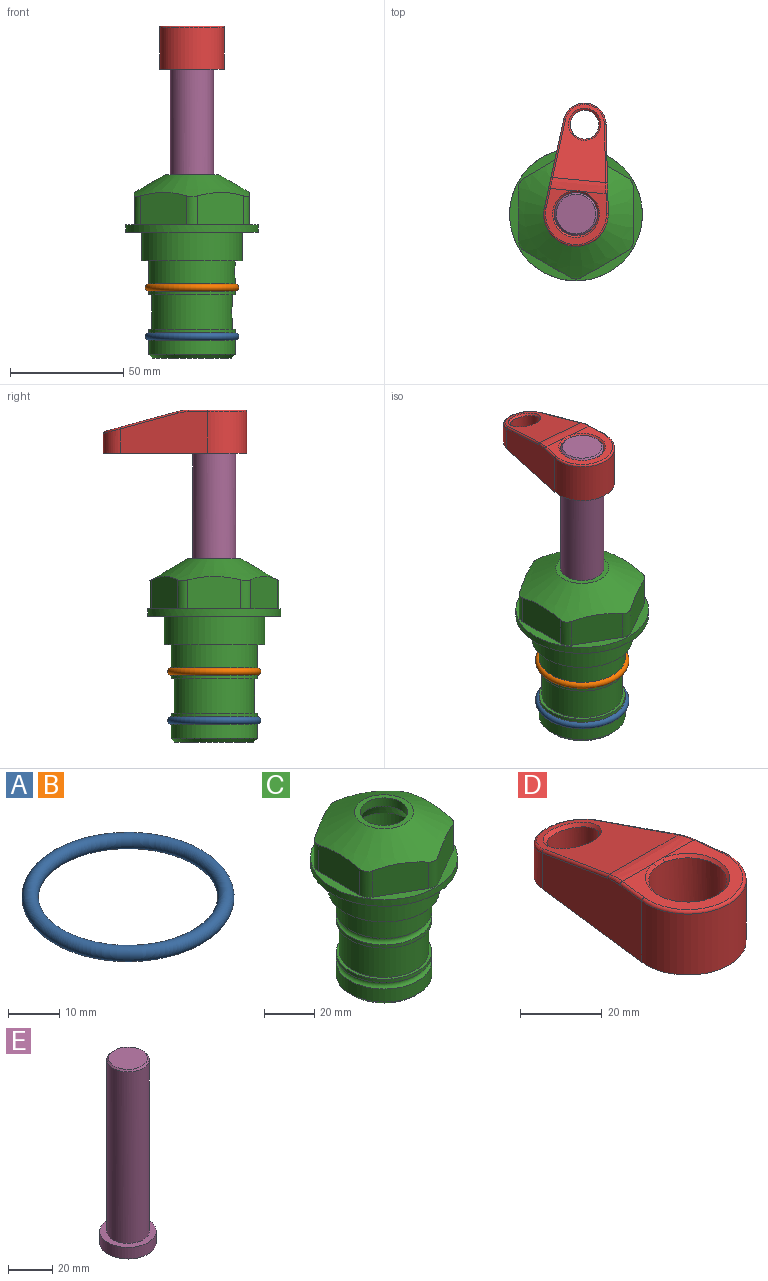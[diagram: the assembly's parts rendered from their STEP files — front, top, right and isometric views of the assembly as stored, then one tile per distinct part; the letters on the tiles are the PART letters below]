
ASSEMBLY  parts=5 mates=4
PART A: 1 faces, bbox 44.7x44.7x3.2 mm
  f0: torus R=19.05mm, axis (0,0,1), area 1193.9mm2
PART B: same geometry as A
PART C: 36 faces, bbox 58.7x58.7x81 mm
  f0: cylinder r=17.78mm len=35.56mm, axis (0,0,1), area 1670.8mm2, adj f23,f24,f31
  f1: cylinder r=19.05mm len=38.1mm, axis (0,0,1), area 1191.9mm2, adj f26,f27,f30
  f2: plane 58.66x58.66mm, normal (0,0,-1), area 1150.6mm2, adj f3,f28
  f3: cylinder r=29.33mm len=58.66mm, axis (0,0,-1), area 585.1mm2, adj f2,f4
  f4: plane 58.66x58.66mm, normal (0,0,1), area 475.9mm2, adj f3,f5,f6,f7,f8,f9,f10,f11
  f5: plane 20.32x14.34mm, normal (-0.5,0.87,0), area 324.4mm2, adj f4,f15,f16,f17
  f6: plane 20.32x14.34mm, normal (0.5,0.87,0), area 324.4mm2, adj f4,f14,f15,f17
  f7: plane 23.48x14.34mm, normal (1,0,0), area 324.4mm2, adj f4,f13,f14,f17
  f8: plane 20.32x14.34mm, normal (0.5,-0.87,0), area 324.4mm2, adj f4,f12,f13,f17
  f9: plane 20.32x14.34mm, normal (-0.5,-0.87,0), area 324.4mm2, adj f4,f11,f12,f17
  f10: plane 23.48x14.34mm, normal (-1,0,0), area 324.4mm2, adj f4,f11,f16,f17
  f11: cylinder r=5.08mm len=12.85mm, axis (0,0,-1), area 67.2mm2, adj f4,f9,f10,f17
  f12: cylinder r=5.08mm len=12.85mm, axis (0,0,-1), area 67.2mm2, adj f4,f8,f9,f17
  f13: cylinder r=5.08mm len=12.85mm, axis (0,0,-1), area 67.2mm2, adj f4,f7,f8,f17
  f14: cylinder r=5.08mm len=12.85mm, axis (0,0,-1), area 67.2mm2, adj f4,f6,f7,f17
  f15: cylinder r=5.08mm len=12.85mm, axis (0,0,-1), area 67.2mm2, adj f4,f5,f6,f17
  f16: cylinder r=5.08mm len=12.85mm, axis (0,0,-1), area 67.2mm2, adj f4,f5,f10,f17
  f17: cone r=11.73mm half-angle=60deg, axis (0,0,-1), area 2071.8mm2, adj f5,f6,f7,f8,f9,f10,f11,f12
  f18: plane 23.46x23.46mm, normal (0,0,1), area 147.4mm2, adj f17,f35
  f19: plane 34.93x34.93mm, normal (0,0,-1), area 958mm2, adj f29
  f20: cylinder r=19.05mm len=38.1mm, axis (0,0,1), area 760.1mm2, adj f21,f29
  f21: torus R=19.05mm, axis (0,0,1), area 565.3mm2, adj f20,f22
  f22: cylinder r=19.05mm len=38.1mm, axis (0,0,1), area 190mm2, adj f21,f23
  f23: plane 38.1x38.1mm, normal (0,0,1), area 146.9mm2, adj f0,f22
  f24: plane 38.1x38.1mm, normal (0,0,-1), area 146.9mm2, adj f0,f25
  f25: cylinder r=19.05mm len=38.1mm, axis (0,0,1), area 190mm2, adj f24,f26
  f26: torus R=19.05mm, axis (0,0,1), area 565.3mm2, adj f1,f25
  f27: plane 44.45x44.45mm, normal (0,0,-1), area 411.7mm2, adj f1,f28
  f28: cylinder r=22.23mm len=44.45mm, axis (0,0,1), area 1773.5mm2, adj f2,f27
  f29: cone r=19.05mm half-angle=45deg, axis (0,0,1), area 257.5mm2, adj f19,f20
  f30: cylinder r=3.17mm len=6.75mm, axis (-1,0,0), area 128mm2, adj f1,f33
  f31: cylinder r=3.17mm len=6.35mm, axis (-1,0,0), area 102.5mm2, adj f0,f33
  f32: plane 25.4x25.4mm, normal (0,0,1), area 506.7mm2, adj f33
  f33: cylinder r=12.7mm len=66.42mm, axis (0,0,-1), area 5236.2mm2, adj f30,f31,f32,f34
  f34: cone r=9.53mm half-angle=30deg, axis (0,0,-1), area 443.4mm2, adj f33,f35
  f35: cylinder r=9.53mm len=19.05mm, axis (0,0,-1), area 240.9mm2, adj f18,f34
PART D: 31 faces, bbox 31.7x65.5x19.8 mm
  f0: plane 39.12x18.26mm, normal (0.99,0.12,0), area 612.2mm2, adj f1,f4,f7,f11,f13,f15
  f1: cylinder r=9.53mm len=18.91mm, axis (0,0,-1), area 296.1mm2, adj f0,f2,f7,f17
  f2: plane 39.12x18.26mm, normal (-0.99,0.12,0), area 612.2mm2, adj f1,f4,f7,f12,f14,f16
  f3: cylinder r=6.35mm len=12.7mm, axis (0,0,-1), area 362.4mm2, adj f7,f18
  f4: cylinder r=14.29mm len=28.58mm, axis (0,0,-1), area 882.2mm2, adj f0,f2,f7,f10
  f5: cylinder r=9.53mm len=19.05mm, axis (0,0,-1), area 1092.6mm2, adj f7,f19,f20
  f6: plane 26.99x23.69mm, normal (0,0,1), area 216.2mm2, adj f9,f10,f11,f12,f19
  f7: plane 63.5x28.58mm, normal (0,0,-1), area 661.8mm2, adj f0,f1,f2,f3,f4,f5,f22,f23
  f8: plane 33.52x23.6mm, normal (0,0.26,0.97), area 486mm2, adj f9,f15,f16,f17,f18
  f9: cylinder r=19.05mm len=24.72mm, axis (1,0,0), area 120.4mm2, adj f6,f8,f13,f14,f20
  f10: torus R=13.49mm, axis (0,0,1), area 59mm2, adj f4,f6,f11,f12
  f11: cylinder r=0.79mm len=8.67mm, axis (0.12,-0.99,0), area 10.8mm2, adj f0,f6,f10,f13
  f12: cylinder r=0.79mm len=8.67mm, axis (0.12,0.99,0), area 10.8mm2, adj f2,f6,f10,f14
  f13: bspline ~4.95x1.42mm, area 6.1mm2, adj f0,f9,f11,f15
  f14: bspline ~4.95x1.42mm, area 6.1mm2, adj f2,f9,f12,f16
  f15: cylinder r=0.79mm len=25.95mm, axis (0.12,-0.96,0.26), area 32.9mm2, adj f0,f8,f13,f17
  f16: cylinder r=0.79mm len=25.95mm, axis (0.12,0.96,-0.26), area 32.9mm2, adj f2,f8,f14,f17
  f17: bspline ~18.91x8.38mm, area 30mm2, adj f1,f8,f15,f16
  f18: bspline ~14.29x14.29mm, area 48.3mm2, adj f3,f8
  f19: cone r=9.53mm half-angle=45deg, axis (0,0,1), area 66.5mm2, adj f5,f6,f20
  f20: bspline ~3.22x0.96mm, area 3.5mm2, adj f5,f9,f19
  f21: plane 2.75x2.72mm, normal (0,0,-1), area 2.9mm2, adj f23,f25,f28
  f22: plane 23.05x15.88mm, normal (-0.99,-0.12,0), area 323.6mm2, adj f7,f25,f26,f27,f28,f29
  f23: plane 23.05x15.88mm, normal (0.99,-0.12,0), area 323.6mm2, adj f7,f21,f25,f27,f28,f30
  f24: cylinder r=9.53mm len=10.69mm, axis (0,0,-1), area 114.7mm2, adj f7,f27,f29,f30
  f25: cylinder r=12.7mm len=20.59mm, axis (0,0,-1), area 381.1mm2, adj f7,f21,f22,f23,f26,f28
  f26: plane 2.75x2.72mm, normal (0,0,-1), area 2.9mm2, adj f22,f25,f28
  f27: plane 19.72x18.37mm, normal (0,-0.26,-0.97), area 291.8mm2, adj f22,f23,f24,f28,f29,f30
  f28: cylinder r=15.88mm len=19.92mm, axis (1,0,0), area 54.8mm2, adj f21,f22,f23,f25,f26,f27
  f29: cylinder r=1.59mm len=11mm, axis (0,0,-1), area 34.7mm2, adj f7,f22,f24,f27
  f30: cylinder r=1.59mm len=11mm, axis (0,0,-1), area 34.7mm2, adj f7,f23,f24,f27
PART E: 6 faces, bbox 25.4x25.4x101.6 mm
  f0: plane 17.46x17.46mm, normal (0,0,1), area 239.5mm2, adj f5
  f1: plane 25.4x25.4mm, normal (0,0,-1), area 506.7mm2, adj f2
  f2: cylinder r=12.7mm len=25.4mm, axis (0,0,1), area 506.7mm2, adj f1,f3
  f3: plane 25.4x25.4mm, normal (0,0,1), area 221.7mm2, adj f2,f4
  f4: cylinder r=9.53mm len=94.46mm, axis (0,0,1), area 5653mm2, adj f3,f5
  f5: cone r=8.73mm half-angle=45deg, axis (0,0,-1), area 64.4mm2, adj f0,f4
PLACE A t=(0,0,-21.59)mm
PLACE B at identity
PLACE C at identity fixed
PLACE D rot(axis=(0,0,-1),5.5deg) t=(0,0,27.55)mm
PLACE E rot(axis=(0,0,-1),5.5deg) t=(0,0,27.55)mm
MATE cylindrical E.f2 <-> C.f0  axis (0,0,-1) through (0,0,-10.55)mm
MATE fastened B.f0 <-> C.f0  axis (0,0,1) through (0,0,-24.51)mm
MATE fastened D.f4 <-> E.f2  axis (0,0,1) through (0,0,91.05)mm
MATE fastened A.f0 <-> C.f0  axis (0,0,1) through (0,0,-46.1)mm
